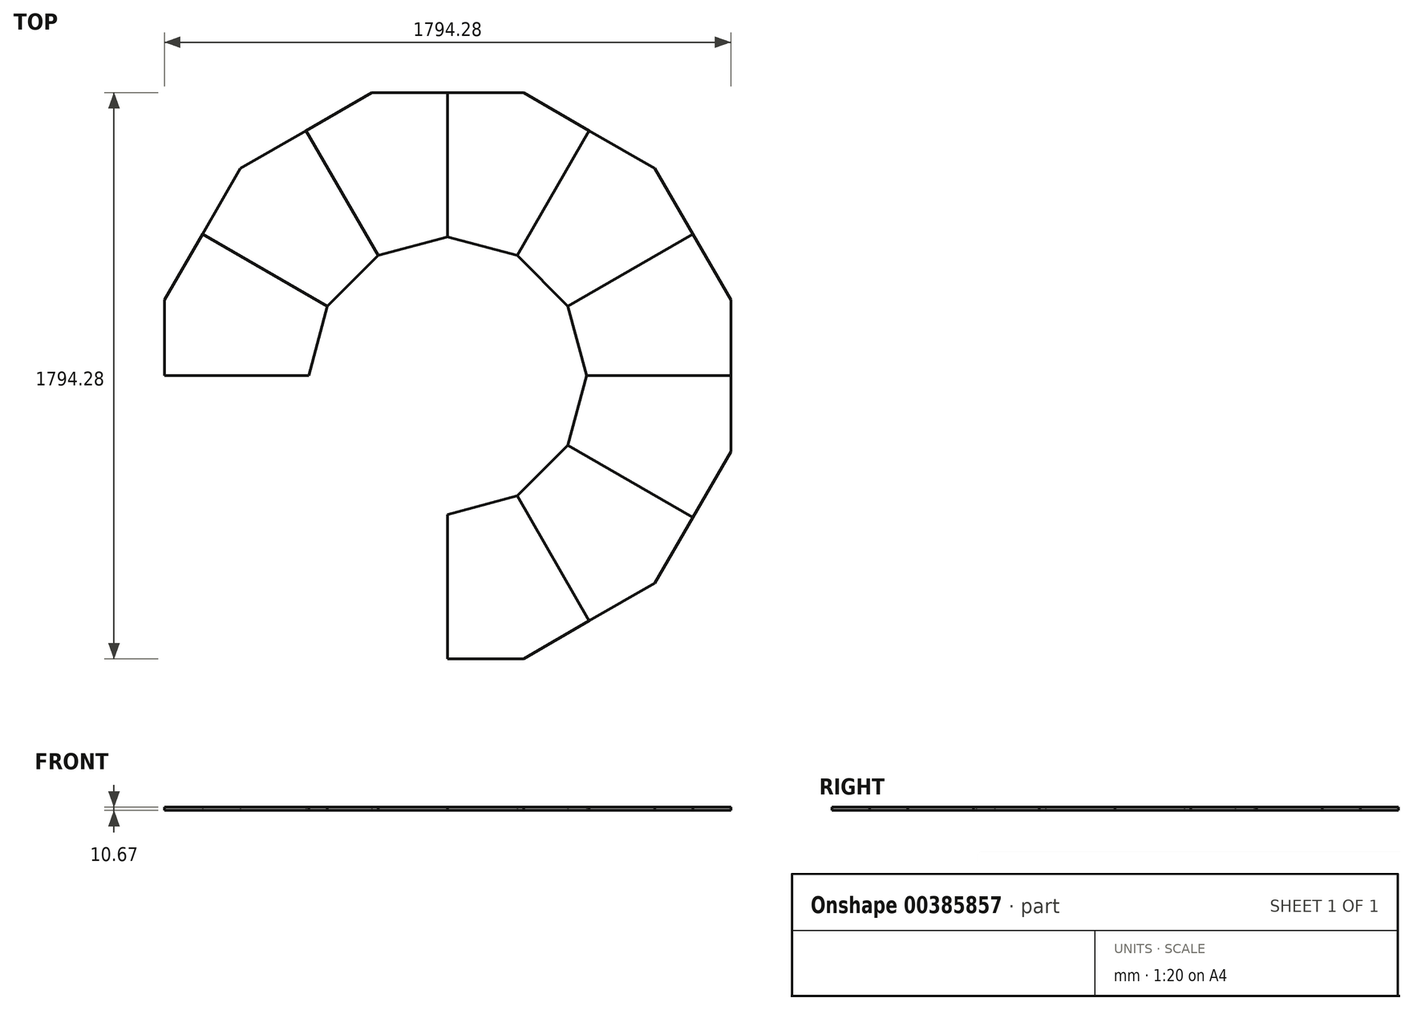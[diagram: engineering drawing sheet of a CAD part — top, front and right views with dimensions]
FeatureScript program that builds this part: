
annotation { "Feature Type Name" : "Feature", "Feature Type Description" : "" }
export const myFeature = defineFeature(function(context is Context, id is Id, definition is map)
    precondition{}
    {
        {
            var Q0;
            Q0=qCreatedBy(makeId("Top.planeOp"),FACE);
            var sketch = newSketch(context, id + "F0", { "sketchPlane" : qUnion([Q0])});
            skCircle(sketch, "E0", {"center": v(0, 0) * mm, "radius": 424.95 * mm, "construction": true});
            skLineSegment(sketch, "E1", {"start": v(-439.94, 0) * mm, "end": v(-897.14, 0) * mm});
            skLineSegment(sketch, "E2", {"start": v(-897.14, 0) * mm, "end": v(-897.14, 240.39) * mm});
            skLineSegment(sketch, "E3", {"start": v(-897.14, 240.39) * mm, "end": v(-776.95, 448.57) * mm});
            skLineSegment(sketch, "E4", {"start": v(-381, 219.97) * mm, "end": v(-439.94, 0) * mm});
            skLineSegment(sketch, "E5", {"start": v(0, 0) * mm, "end": v(-439.94, 0) * mm, "construction": true});
            skLineSegment(sketch, "E6", {"start": v(0, 0) * mm, "end": v(-381, 219.97) * mm, "construction": true});
            skPoint(sketch, "E7.start.orphan", {"position": v(0, 1794.28) * mm});
            skLineSegment(sketch, "E8", {"start": v(-381, 219.97) * mm, "end": v(-776.95, 448.57) * mm});
            skLineSegment(sketch, "E9", {"start": v(-897.14, 240.39) * mm, "end": v(0, 0) * mm, "construction": true});
            skPoint(sketch, "E10.orphan", {"position": v(-410.47, 109.99) * mm});
            skLineSegment(sketch, "E11", {"start": v(-439.94, 0) * mm, "end": v(-439.94, 254) * mm, "construction": true});
            skLineSegment(sketch, "E12.1.0", {"start": v(-656.75, 656.75) * mm, "end": v(-448.57, 776.95) * mm});
            skLineSegment(sketch, "E12.1.1", {"start": v(-219.97, 381) * mm, "end": v(-381, 219.97) * mm});
            skLineSegment(sketch, "E12.1.2", {"start": v(-219.97, 381) * mm, "end": v(-448.57, 776.95) * mm});
            skLineSegment(sketch, "E12.1.4", {"start": v(-776.95, 448.57) * mm, "end": v(-656.75, 656.75) * mm});
            skLineSegment(sketch, "E12.2.0", {"start": v(-240.39, 897.14) * mm, "end": v(0, 897.14) * mm});
            skLineSegment(sketch, "E12.2.1", {"start": v(0, 439.94) * mm, "end": v(-219.97, 381) * mm});
            skLineSegment(sketch, "E12.2.2", {"start": v(0, 439.94) * mm, "end": v(0, 897.14) * mm});
            skLineSegment(sketch, "E12.2.3", {"start": v(-219.97, 381) * mm, "end": v(-448.57, 776.95) * mm});
            skLineSegment(sketch, "E12.2.4", {"start": v(-448.57, 776.95) * mm, "end": v(-240.39, 897.14) * mm});
            skLineSegment(sketch, "E12.3.0", {"start": v(240.39, 897.14) * mm, "end": v(448.57, 776.95) * mm});
            skLineSegment(sketch, "E12.3.1", {"start": v(219.97, 381) * mm, "end": v(0, 439.94) * mm});
            skLineSegment(sketch, "E12.3.2", {"start": v(219.97, 381) * mm, "end": v(448.57, 776.95) * mm});
            skLineSegment(sketch, "E12.3.3", {"start": v(0, 439.94) * mm, "end": v(0, 897.14) * mm});
            skLineSegment(sketch, "E12.3.4", {"start": v(0, 897.14) * mm, "end": v(240.39, 897.14) * mm});
            skLineSegment(sketch, "E12.4.0", {"start": v(656.75, 656.75) * mm, "end": v(776.95, 448.57) * mm});
            skLineSegment(sketch, "E12.4.1", {"start": v(381, 219.97) * mm, "end": v(219.97, 381) * mm});
            skLineSegment(sketch, "E12.4.2", {"start": v(381, 219.97) * mm, "end": v(776.95, 448.57) * mm});
            skLineSegment(sketch, "E12.4.3", {"start": v(219.97, 381) * mm, "end": v(448.57, 776.95) * mm});
            skLineSegment(sketch, "E12.4.4", {"start": v(448.57, 776.95) * mm, "end": v(656.75, 656.75) * mm});
            skLineSegment(sketch, "E12.5.0", {"start": v(897.14, 240.39) * mm, "end": v(897.14, 0) * mm});
            skLineSegment(sketch, "E12.5.1", {"start": v(439.94, 0) * mm, "end": v(381, 219.97) * mm});
            skLineSegment(sketch, "E12.5.2", {"start": v(439.94, 0) * mm, "end": v(897.14, 0) * mm});
            skLineSegment(sketch, "E12.5.3", {"start": v(381, 219.97) * mm, "end": v(776.95, 448.57) * mm});
            skLineSegment(sketch, "E12.5.4", {"start": v(776.95, 448.57) * mm, "end": v(897.14, 240.39) * mm});
            skLineSegment(sketch, "E12.6.0", {"start": v(897.14, -240.39) * mm, "end": v(776.95, -448.57) * mm});
            skLineSegment(sketch, "E12.6.1", {"start": v(381, -219.97) * mm, "end": v(439.94, 0) * mm});
            skLineSegment(sketch, "E12.6.2", {"start": v(381, -219.97) * mm, "end": v(776.95, -448.57) * mm});
            skLineSegment(sketch, "E12.6.3", {"start": v(439.94, 0) * mm, "end": v(897.14, 0) * mm});
            skLineSegment(sketch, "E12.6.4", {"start": v(897.14, 0) * mm, "end": v(897.14, -240.39) * mm});
            skLineSegment(sketch, "E12.7.0", {"start": v(656.75, -656.75) * mm, "end": v(448.57, -776.95) * mm});
            skLineSegment(sketch, "E12.7.1", {"start": v(219.97, -381) * mm, "end": v(381, -219.97) * mm});
            skLineSegment(sketch, "E12.7.2", {"start": v(219.97, -381) * mm, "end": v(448.57, -776.95) * mm});
            skLineSegment(sketch, "E12.7.3", {"start": v(381, -219.97) * mm, "end": v(776.95, -448.57) * mm});
            skLineSegment(sketch, "E12.7.4", {"start": v(776.95, -448.57) * mm, "end": v(656.75, -656.75) * mm});
            skLineSegment(sketch, "E12.8.0", {"start": v(240.39, -897.14) * mm, "end": v(0, -897.14) * mm});
            skLineSegment(sketch, "E12.8.1", {"start": v(0, -439.94) * mm, "end": v(219.97, -381) * mm});
            skLineSegment(sketch, "E12.8.2", {"start": v(0, -439.94) * mm, "end": v(0, -897.14) * mm});
            skLineSegment(sketch, "E12.8.3", {"start": v(219.97, -381) * mm, "end": v(448.57, -776.95) * mm});
            skLineSegment(sketch, "E12.8.4", {"start": v(448.57, -776.95) * mm, "end": v(240.39, -897.14) * mm});
            skLineSegment(sketch, "E12.anchor1", {"start": v(0, 0) * mm, "end": v(-897.14, 240.39) * mm, "construction": true});
            skLineSegment(sketch, "E12.anchor2", {"start": v(0, 0) * mm, "end": v(240.39, -897.14) * mm, "construction": true});
            skSolve(sketch);
        }
        {
            assignVariable(context, id + "F1", {"name" : "rise", "anyValue" : 96 / 9});
        }
        {
            var Q0;
            Q0=makeQuery(id+"F0.imprint","IMPRINT",FACE,{"disambiguationData":[TD([[makeQuery(id+"F0.imprint","IMPRINT",EDGE,{"derivedFrom":sQuery(id+"F0.wireOp",EDGE,"E1")}),-1.0]])]});
            extrude(context, id + "F2", {"entities" : qUnion([Q0]), "depth" : (getVariable(context, 'rise')) * mm});
        }
        {
            var Q0;
            Q0=qCreatedBy(makeId("Right.planeOp"),FACE);
            var sketch = newSketch(context, id + "F3", { "sketchPlane" : qUnion([Q0])});
            skLineSegment(sketch, "E13", {"start": v(0, 0) * mm, "end": v(0, 347.06) * mm});
            skSolve(sketch);
        }
        {
            var Q0;
            Q0=makeQuery(id+"F2.opExtrude","SWEPT_BODY",BODY,{"disambiguationData":[OSD([sQuery(id+"F0.wireOp",EDGE,"E1"),sQuery(id+"F0.wireOp",EDGE,"E2"),sQuery(id+"F0.wireOp",EDGE,"E3"),sQuery(id+"F0.wireOp",EDGE,"E4"),sQuery(id+"F0.wireOp",EDGE,"E8")])]});
            var Q1;
            Q1=sQuery(id+"F3.wireOp",EDGE,"E13");
            circularPattern(context, id + "F4", {"entities" : qUnion([Q0]), "axis" : qUnion([Q1]), "angle" : 240 * degree, "instanceCount" : 9, "oppositeDirection" : true, "equalSpace" : true});
        }
    });
